# Revit family: BOS-Sino-Zarge-osd-STW_Familie
name_source: partatom
category: Türen
revit_build: Autodesk Revit 2017 (Build: 20160225_1515(x64)
units: mm (PartAtom-declared; Revit-internal decimal feet)

## family parameters
Basisbauteil = Wand
Beim Laden mit Abzugskörper schneiden = Nein
Gemeinsam genutzt = Nein
Immer vertikal = Ja
Raumberechnungspunkt = Ja

## types (5) — shared parameters
AK-Aussteifungsprofilabstand = 104 mm  [stored 0.341207 ft]
BBL1 Bandbezugslinie   Hinge Position 1 = 241 mm  [stored 0.790682 ft]
BE max. = 100 mm  [stored 0.328084 ft]
Bauelement = BOS Stahlzarge
Blechstärke = 2 mm  [stored 0.00656168 ft]
Dichtung 1 = Ja
Drehpunkt Warnung sichtbar = Ja
Drehpunktreferenz horizontal = 500 mm  [stored 1.64042 ft]
Einfügepunkt = 54 mm  [stored 0.177165 ft]
FMB max. = 966 mm  [stored 3.16929 ft]
FMB min. = 591 mm  [stored 1.93898 ft]
FMH max. = 2358 mm  [stored 7.73622 ft]
FMH min. = 1608 mm  [stored 5.27559 ft]
Falzaufschlag = 15 mm  [stored 0.0492126 ft]
Funktion = Innen
GT max. = 336 mm  [stored 1.10236 ft]
Gefälzt = Nein
Hersteller = BOS GmbH Best Of Steel, Lütkenfelde 4, D-48282 Emsdetten
Info-Texte sichtbar = Ja
Information in English = Nein
Material = grundiert, feuerverzinktes Feinblech nach DIN EN 10143
Material - Acrylfuge = <Nach Kategorie>
Material - Bänder = <Nach Kategorie>
Material - Dichtung = <Nach Kategorie>
Material - Drückergarnitur = <Nach Kategorie>
Material - Türblatt = <Nach Kategorie>
Material - Zarge = <Nach Kategorie>
Modell = osd
Putzwinkel max. = 3 mm  [stored 0.00984252 ft]
Putzwinkel min. = 3 mm  [stored 0.00984252 ft]
Sickentiefe = 10 mm  [stored 0.0328084 ft]
Spiegel hinten max. = 4 mm  [stored 0.0131234 ft]
Spiegel hinten min. = 4 mm  [stored 0.0131234 ft]
Spiegel vorne max. = 4 mm  [stored 0.0131234 ft]
Spiegel vorne min. = 4 mm  [stored 0.0131234 ft]
Stumpf = Ja
Technische Infos rund um die Stahlzarge = www.BestOfSteel.de/tools-downloads/technische-infos-rund-um-die-stahlzarge/
Typenbild = <Keine Auswahl>
Türblattabstand 2 = 4.5 mm  [stored 0.0147638 ft]
Türblattabstand 3 = 4.5 mm  [stored 0.0147638 ft]
Türblattabstand links-rechts = 3.5 mm  [stored 0.0114829 ft]
Türblattabstand oben = 4 mm  [stored 0.0131234 ft]
Türblattabstand unten = 7 mm  [stored 0.0229659 ft]
Türblattaufschlag = 13 mm
URL = www.BestOfSteel.de/stahlzargen/zargen-fuer-drehfluegeltueren/sino-zargen/
Öffnungswinkel max. = 180.00°
Öffnungswinkel min. = 0.00°
zero-valued in all types: Breite, Dicke, Rohbaubreite, Rohbauhöhe

## per-type parameters (varying)
| type | Beschreibung | Dichtung 2 | Doppelfalz | Einfachfalz | Falzaufschlag gesamt | MW min. | osFd mit Holztürblatt (Bandrolle sichtbar) | osFd mit Holztürblatt (verdeckt liegendes Band) | osd mit Glastürblatt | osd mit Holztürblatt (Bandrolle sichtbar) | osd mit Holztürblatt (verdeckt liegendes Band) |
| osd mit Holztürblatt (Bandrolle sichtbar) | Sino-Zarge für Ständerwerk, stumpf | Nein | Nein | Ja | 15 mm  [stored 0.0492126 ft] | 100 mm  [stored 0.328084 ft] | Nein | Nein | Nein | Ja | Nein |
| osFd mit Holztürblatt (verdeckt liegendes Band) | Sino-Zarge für Ständerwerk, stumpf, mit Doppelfalz | Ja | Ja | Nein | 30 mm  [stored 0.0984252 ft] | 125 mm  [stored 0.410105 ft] | Nein | Ja | Nein | Nein | Nein |
| osd mit Holztürblatt (verdeckt liegendes Band) | Sino-Zarge für Ständerwerk, stumpf | Nein | Nein | Ja | 15 mm  [stored 0.0492126 ft] | 100 mm  [stored 0.328084 ft] | Nein | Nein | Nein | Nein | Ja |
| osd mit Glastürblatt | Sino-Zarge für Ständerwerk, stumpf | Nein | Nein | Ja | 15 mm  [stored 0.0492126 ft] | 100 mm  [stored 0.328084 ft] | Nein | Nein | Ja | Nein | Nein |
| osFd mit Holztürblatt (Bandrolle sichtbar) | Sino-Zarge für Ständerwerk, stumpf, mit Doppelfalz | Ja | Ja | Nein | 30 mm  [stored 0.0984252 ft] | 125 mm  [stored 0.410105 ft] | Ja | Nein | Nein | Nein | Nein |

note: [stored X ft] marks values corroborated as IEEE doubles in the binary element streams (Revit-internal decimal feet)

## geometry (parser evidence)
native form markers: Extrusion x8
no freeform markers — native parametric forms only
